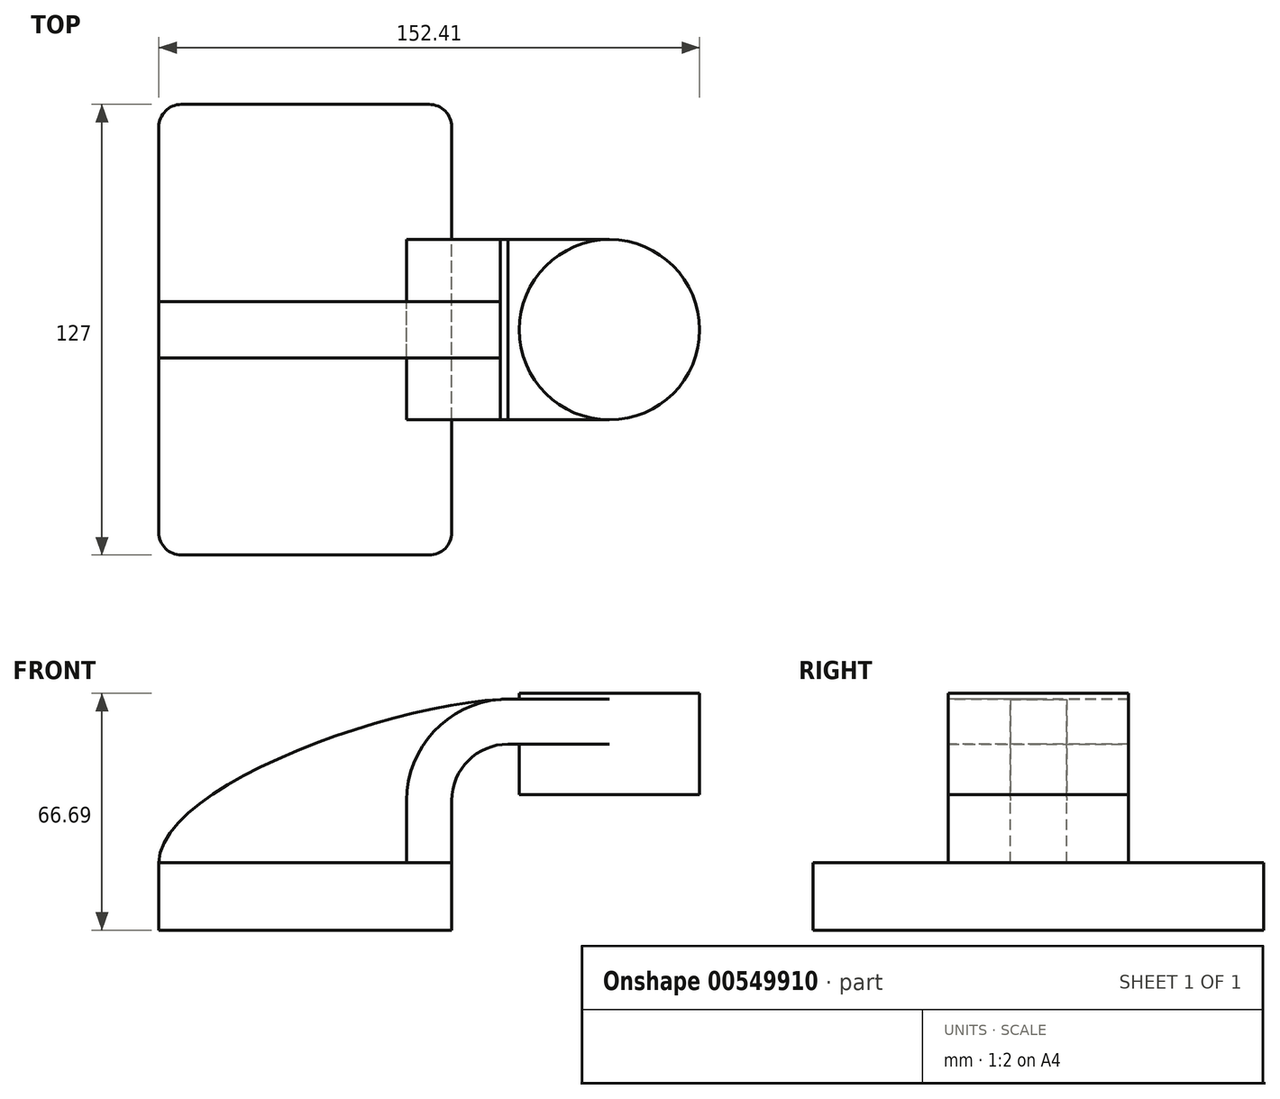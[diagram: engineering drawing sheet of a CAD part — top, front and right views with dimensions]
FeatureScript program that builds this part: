
annotation { "Feature Type Name" : "Feature", "Feature Type Description" : "" }
export const myFeature = defineFeature(function(context is Context, id is Id, definition is map)
    precondition{}
    {
        {
            var Q0;
            Q0=qCreatedBy(makeId("Front.planeOp"),FACE);
            var sketch = newSketch(context, id + "F0", { "sketchPlane" : qUnion([Q0])});
            skLineSegment(sketch, "E0.bottom", {"start": v(-41.27, -9.53) * mm, "end": v(41.28, -9.53) * mm});
            skLineSegment(sketch, "E0.top", {"start": v(-41.28, 9.52) * mm, "end": v(41.28, 9.52) * mm});
            skLineSegment(sketch, "E0.left", {"start": v(-41.28, -9.53) * mm, "end": v(-41.28, 9.52) * mm});
            skLineSegment(sketch, "E0.right", {"start": v(41.28, -9.53) * mm, "end": v(41.28, 9.52) * mm});
            skPoint(sketch, "E0.middle", {"position": v(0, 0) * mm});
            skLineSegment(sketch, "E1.bottom", {"start": v(60.33, 57.16) * mm, "end": v(111.12, 57.16) * mm});
            skLineSegment(sketch, "E1.top", {"start": v(60.33, 28.59) * mm, "end": v(111.12, 28.59) * mm});
            skLineSegment(sketch, "E1.left", {"start": v(60.33, 57.16) * mm, "end": v(60.33, 28.59) * mm});
            skLineSegment(sketch, "E1.right", {"start": v(111.12, 57.16) * mm, "end": v(111.12, 28.59) * mm});
            skPoint(sketch, "E1.middle", {"position": v(85.73, 42.88) * mm});
            skLineSegment(sketch, "E2", {"start": v(41.27, 9.52) * mm, "end": v(41.27, 27) * mm});
            skArc(sketch, "E3", {"start": v(41.27, 27) * mm, "mid": v(45.92, 38.23) * mm, "end": v(57.15, 42.88) * mm});
            skLineSegment(sketch, "E4", {"start": v(57.15, 42.88) * mm, "end": v(85.73, 42.88) * mm});
            skLineSegment(sketch, "E5.0", {"start": v(57.15, 55.58) * mm, "end": v(85.73, 55.58) * mm});
            skArc(sketch, "E5.1", {"start": v(28.57, 27) * mm, "mid": v(36.94, 47.2) * mm, "end": v(57.15, 55.58) * mm});
            skLineSegment(sketch, "E5.2", {"start": v(28.57, 9.52) * mm, "end": v(28.57, 27) * mm});
            skLineSegment(sketch, "E6", {"start": v(85.73, 28.59) * mm, "end": v(85.73, 57.16) * mm});
            skFitSpline(sketch, "E7", {"points": [v(-41.28, 9.53) * mm, v(57.15, 55.58) * mm], "startDerivative": vector(0.74, 65.56) * mm, "endDerivative": vector(93.74, 2.17) * mm});
            skSolve(sketch);
        }
        {
            var Q0;
            Q0=makeQuery(id+"F0.imprint","IMPRINT",FACE,{"disambiguationData":[TD([[makeQuery(id+"F0.imprint","IMPRINT",EDGE,{"derivedFrom":sQuery(id+"F0.wireOp",EDGE,"E0.bottom")}),1.0]])]});
            extrude(context, id + "F1", {"entities" : qUnion([Q0]), "endBound" : BoundingType.SYMMETRIC, "depth" : 127 * mm, "offsetDistance" : 25.4 * mm});
        }
        {
            var Q0;
            {var subQ1=sQuery(id+"F0.wireOp",EDGE,"E2");Q0=makeQuery(id+"F0.imprint","IMPRINT",FACE,{"disambiguationData":[TD([[makeQuery(id+"F0.imprint","IMPRINT",EDGE,{"derivedFrom":subQ1}),1.0]])]});}
            var Q1;
            {var subQ0=sQuery(id+"F0.wireOp",EDGE,"E5.0");var subQ1=sQuery(id+"F0.wireOp",EDGE,"E1.left");var subQ2=makeQuery(id+"F0.imprint","INTERSECT",VERTEX,{"derivedFrom":[subQ1,subQ0]});Q1=makeQuery(id+"F0.imprint","IMPRINT",FACE,{"disambiguationData":[TD([[makeQuery(id+"F0.imprint","IMPRINT",EDGE,{"disambiguationData":[TD([[subQ2,-1.0]])],"derivedFrom":subQ1}),1.0]])]});}
            extrude(context, id + "F2", {"entities" : qUnion([Q0, Q1]), "endBound" : BoundingType.SYMMETRIC, "depth" : 50.8 * mm, "offsetDistance" : 25.4 * mm});
        }
        {
            var Q0;
            {var subQ3=sQuery(id+"F0.wireOp",EDGE,"E5.2");Q0=makeQuery(id+"F0.imprint","IMPRINT",FACE,{"disambiguationData":[TD([[makeQuery(id+"F0.imprint","IMPRINT",EDGE,{"derivedFrom":subQ3}),1.0]])]});}
            extrude(context, id + "F3", {"entities" : qUnion([Q0]), "endBound" : BoundingType.SYMMETRIC, "depth" : 15.88 * mm, "offsetDistance" : 25.4 * mm});
        }
        {
            var Q0;
            {var subQ4=sQuery(id+"F0.wireOp",EDGE,"E1.right");Q0=makeQuery(id+"F0.imprint","IMPRINT",FACE,{"disambiguationData":[TD([[makeQuery(id+"F0.imprint","IMPRINT",EDGE,{"derivedFrom":subQ4}),-1.0]])]});}
            var Q1;
            Q1=sQuery(id+"F0.wireOp",EDGE,"E6");
            revolve(context, id + "F4", {"operationType" : NewBodyOperationType.ADD, "entities" : qUnion([Q0]), "axis" : qUnion([Q1]), "revolveType" : RevolveType.FULL});
        }
        {
            var Q0;
            Q0=makeQuery(id+"F1.opExtrude","CAP_EDGE",EDGE,{"disambiguationData":[OSD([sQuery(id+"F0.wireOp",EDGE,"E0.right")])],"isStart":false});
            var Q1;
            Q1=makeQuery(id+"F1.opExtrude","CAP_EDGE",EDGE,{"disambiguationData":[OSD([sQuery(id+"F0.wireOp",EDGE,"E0.left")])],"isStart":false});
            var Q2;
            Q2=makeQuery(id+"F1.opExtrude","CAP_EDGE",EDGE,{"disambiguationData":[OSD([sQuery(id+"F0.wireOp",EDGE,"E0.right")])],"isStart":true});
            var Q3;
            Q3=makeQuery(id+"F1.opExtrude","CAP_EDGE",EDGE,{"disambiguationData":[OSD([sQuery(id+"F0.wireOp",EDGE,"E0.left")])],"isStart":true});
            fillet(context, id + "F5", {"entities" : qUnion([Q0, Q1, Q2, Q3]), "radius" : 6.35 * mm, "tangentPropagation" : true, "allowEdgeOverflow" : false});
        }
    });
